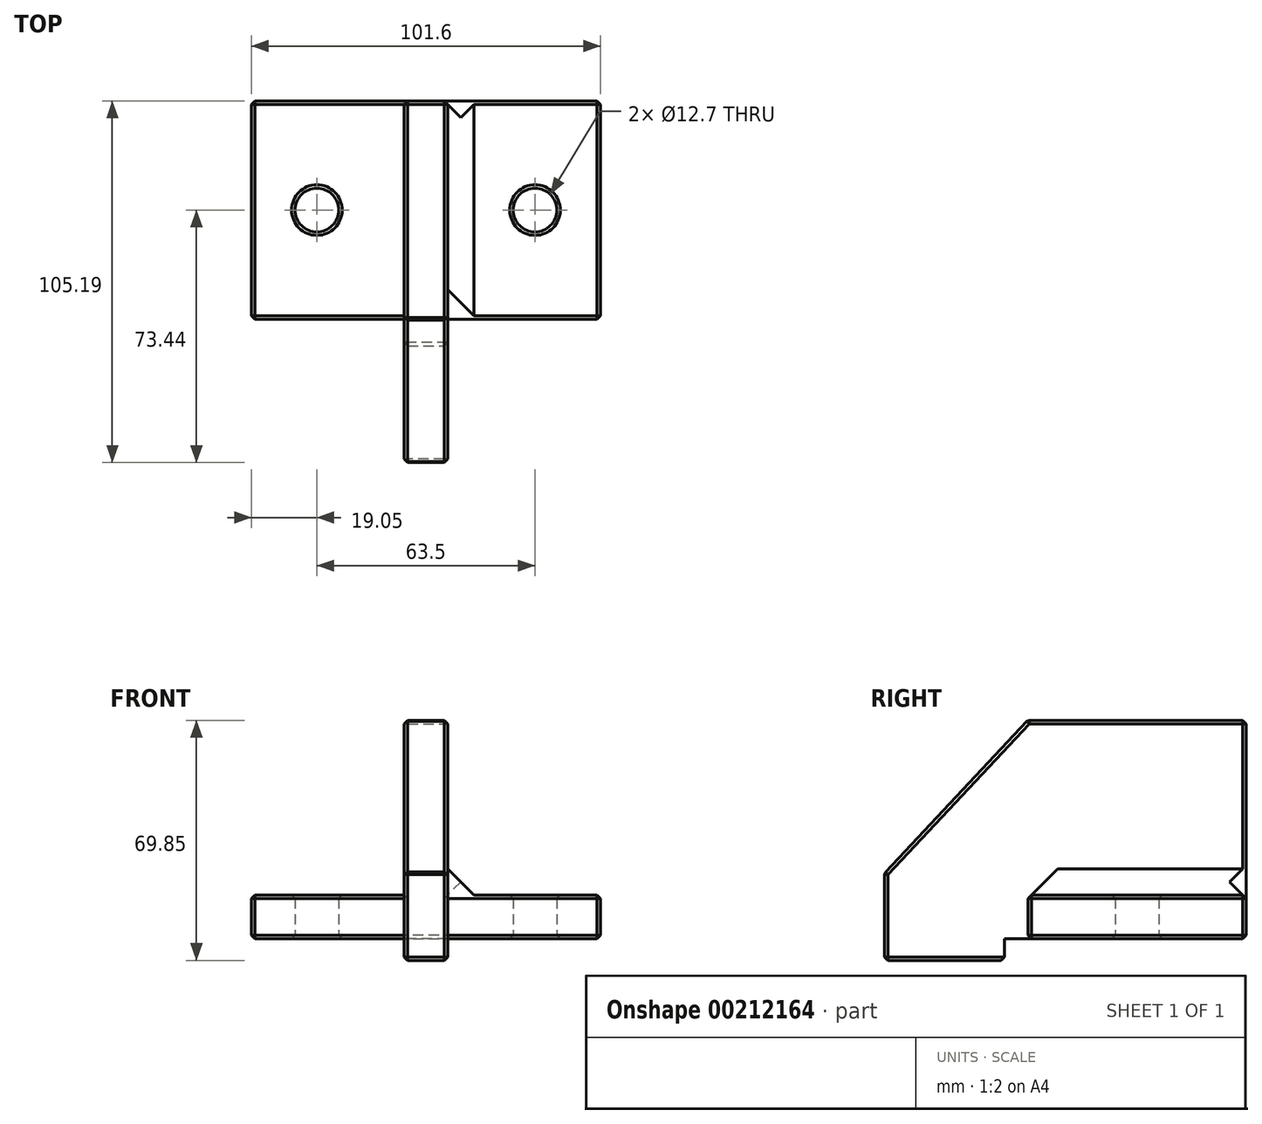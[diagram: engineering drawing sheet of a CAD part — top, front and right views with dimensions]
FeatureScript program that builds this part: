
annotation { "Feature Type Name" : "Feature", "Feature Type Description" : "" }
export const myFeature = defineFeature(function(context is Context, id is Id, definition is map)
    precondition{}
    {
        {
            var Q0;
            Q0=qCreatedBy(makeId("Top.planeOp"),FACE);
            var sketch = newSketch(context, id + "F0", { "sketchPlane" : qUnion([Q0])});
            skLineSegment(sketch, "E0.bottom", {"start": v(50.8, -31.75) * mm, "end": v(-50.8, -31.75) * mm});
            skLineSegment(sketch, "E0.top", {"start": v(50.8, 31.75) * mm, "end": v(-50.8, 31.75) * mm});
            skLineSegment(sketch, "E0.left", {"start": v(50.8, -31.75) * mm, "end": v(50.8, 31.75) * mm});
            skLineSegment(sketch, "E0.right", {"start": v(-50.8, -31.75) * mm, "end": v(-50.8, 31.75) * mm});
            skPoint(sketch, "E0.middle", {"position": v(0, 0) * mm});
            skCircle(sketch, "E1", {"center": v(-31.75, 0) * mm, "radius": 6.35 * mm});
            skCircle(sketch, "E2", {"center": v(31.75, 0) * mm, "radius": 6.35 * mm});
            skLineSegment(sketch, "E3", {"start": v(0, 0) * mm, "end": v(31.75, 0) * mm, "construction": true});
            skLineSegment(sketch, "E4", {"start": v(0, 0) * mm, "end": v(-31.75, 0) * mm, "construction": true});
            skSolve(sketch);
        }
        {
            var Q0;
            Q0=makeQuery(id+"F0.imprint","IMPRINT",FACE,{"disambiguationData":[TD([[makeQuery(id+"F0.imprint","IMPRINT",EDGE,{"derivedFrom":sQuery(id+"F0.wireOp",EDGE,"E0.bottom")}),-1.0]])]});
            extrude(context, id + "F1", {"entities" : qUnion([Q0]), "depth" : 12.7 * mm});
        }
        {
            var Q0;
            Q0=makeQuery(id+"F1.opExtrude","SWEPT_FACE",FACE,{"disambiguationData":[OSD([sQuery(id+"F0.wireOp",EDGE,"E0.right")])]});
            var sketch = newSketch(context, id + "F2", { "sketchPlane" : qUnion([Q0])});
            skLineSegment(sketch, "E5", {"start": v(-31.75, 12.7) * mm, "end": v(-31.75, 63.5) * mm});
            skLineSegment(sketch, "E6", {"start": v(-31.75, 63.5) * mm, "end": v(31.75, 63.5) * mm});
            skLineSegment(sketch, "E7", {"start": v(31.75, 63.5) * mm, "end": v(73.44, 19.05) * mm});
            skLineSegment(sketch, "E8", {"start": v(73.44, 19.05) * mm, "end": v(73.44, -6.35) * mm});
            skLineSegment(sketch, "E9", {"start": v(73.44, -6.35) * mm, "end": v(38.51, -6.35) * mm});
            skLineSegment(sketch, "E10", {"start": v(38.51, -6.35) * mm, "end": v(38.51, 0) * mm});
            skLineSegment(sketch, "E11", {"start": v(38.51, 0) * mm, "end": v(31.75, 0) * mm});
            skSolve(sketch);
        }
        {
            var Q0;
            Q0=makeQuery(id+"F2.imprint","IMPRINT",FACE,{"disambiguationData":[TD([[makeQuery(id+"F2.imprint","IMPRINT",EDGE,{"derivedFrom":sQuery(id+"F2.wireOp",EDGE,"E5")}),-1.0]])]});
            extrude(context, id + "F3", {"entities" : qUnion([Q0]), "operationType" : NewBodyOperationType.ADD, "oppositeDirection" : true, "depth" : 57.15 * mm, "hasSecondDirection" : true, "secondDirectionOppositeDirection" : true, "secondDirectionDepth" : 44.45 * mm});
        }
        {
            var Q0;
            Q0=makeQuery(id+"F3.opExtrude","SWEPT_EDGE",EDGE,{"disambiguationData":[OSD([sQuery(id+"F2.wireOp",EDGE,"E9"),sQuery(id+"F2.wireOp",EDGE,"E10")])]});
            var Q1;
            Q1=makeQuery(id+"F3.opExtrude","CAP_EDGE",EDGE,{"disambiguationData":[OSD([sQuery(id+"F2.wireOp",EDGE,"E9")])],"isStart":false});
            var Q2;
            Q2=makeQuery(id+"F3.opExtrude","CAP_EDGE",EDGE,{"disambiguationData":[OSD([sQuery(id+"F2.wireOp",EDGE,"E9")])],"isStart":true});
            var Q3;
            Q3=makeQuery(id+"F3.opExtrude","SWEPT_FACE",FACE,{"disambiguationData":[OSD([sQuery(id+"F2.wireOp",EDGE,"E8")])]});
            var Q4;
            Q4=makeQuery(id+"F3.opExtrude","SWEPT_FACE",FACE,{"disambiguationData":[OSD([sQuery(id+"F2.wireOp",EDGE,"E7")])]});
            var Q5;
            Q5=makeQuery(id+"F3.opExtrude","SWEPT_FACE",FACE,{"disambiguationData":[OSD([sQuery(id+"F2.wireOp",EDGE,"E6")])]});
            var Q6;
            Q6=makeQuery(id+"F3.boolean.opBoolean","MERGE",FACE,{"derivedFrom":[makeQuery(id+"F1.opExtrude","SWEPT_FACE",FACE,{"disambiguationData":[OSD([sQuery(id+"F0.wireOp",EDGE,"E0.top")])]}),makeQuery(id+"F3.opExtrude","SWEPT_FACE",FACE,{"disambiguationData":[OSD([sQuery(id+"F2.wireOp",EDGE,"E5")])]})]});
            var Q7;
            Q7=makeQuery(id+"F1.opExtrude","SWEPT_FACE",FACE,{"disambiguationData":[OSD([sQuery(id+"F0.wireOp",EDGE,"E0.right")])]});
            var Q8;
            {var subQ0=sQuery(id+"F0.wireOp",EDGE,"E0.bottom");var subQ1=sQuery(id+"F0.wireOp",EDGE,"E0.right");Q8=makeQuery(id+"F3.boolean.opBoolean","SPLIT",EDGE,{"disambiguationData":[TD([makeQuery(id+"F1.opExtrude","SWEPT_FACE",FACE,{"disambiguationData":[OSD([subQ1])]})])],"derivedFrom":makeQuery(id+"F1.opExtrude","CAP_EDGE",EDGE,{"disambiguationData":[OSD([subQ0])],"isStart":false})});}
            var Q9;
            {var subQ0=sQuery(id+"F0.wireOp",EDGE,"E0.bottom");var subQ1=sQuery(id+"F0.wireOp",EDGE,"E0.right");Q9=makeQuery(id+"F3.boolean.opBoolean","SPLIT",EDGE,{"disambiguationData":[TD([makeQuery(id+"F1.opExtrude","SWEPT_FACE",FACE,{"disambiguationData":[OSD([subQ1])]})])],"derivedFrom":makeQuery(id+"F1.opExtrude","CAP_EDGE",EDGE,{"disambiguationData":[OSD([subQ0])],"isStart":true})});}
            var Q10;
            Q10=makeQuery(id+"F1.opExtrude","SWEPT_FACE",FACE,{"disambiguationData":[OSD([sQuery(id+"F0.wireOp",EDGE,"E1")])]});
            var Q11;
            Q11=makeQuery(id+"F1.opExtrude","SWEPT_FACE",FACE,{"disambiguationData":[OSD([sQuery(id+"F0.wireOp",EDGE,"E2")])]});
            var Q12;
            {var subQ0=sQuery(id+"F0.wireOp",EDGE,"E0.bottom");var subQ2=sQuery(id+"F0.wireOp",EDGE,"E0.left");Q12=makeQuery(id+"F3.boolean.opBoolean","SPLIT",EDGE,{"disambiguationData":[TD([makeQuery(id+"F1.opExtrude","SWEPT_FACE",FACE,{"disambiguationData":[OSD([subQ2])]})])],"derivedFrom":makeQuery(id+"F1.opExtrude","CAP_EDGE",EDGE,{"disambiguationData":[OSD([subQ0])],"isStart":true})});}
            var Q13;
            Q13=makeQuery(id+"F1.opExtrude","SWEPT_EDGE",EDGE,{"disambiguationData":[OSD([sQuery(id+"F0.wireOp",EDGE,"E0.bottom"),sQuery(id+"F0.wireOp",EDGE,"E0.left")])]});
            var Q14;
            {var subQ0=sQuery(id+"F0.wireOp",EDGE,"E0.bottom");var subQ2=sQuery(id+"F0.wireOp",EDGE,"E0.left");Q14=makeQuery(id+"F3.boolean.opBoolean","SPLIT",EDGE,{"disambiguationData":[TD([makeQuery(id+"F1.opExtrude","SWEPT_FACE",FACE,{"disambiguationData":[OSD([subQ2])]})])],"derivedFrom":makeQuery(id+"F1.opExtrude","CAP_EDGE",EDGE,{"disambiguationData":[OSD([subQ0])],"isStart":false})});}
            var Q15;
            Q15=makeQuery(id+"F1.opExtrude","SWEPT_FACE",FACE,{"disambiguationData":[OSD([sQuery(id+"F0.wireOp",EDGE,"E0.left")])]});
            chamfer(context, id + "F4", {"entities" : qUnion([Q0, Q1, Q2, Q3, Q4, Q5, Q6, Q7, Q8, Q9, Q10, Q11, Q12, Q13, Q14, Q15]), "width" : 1.02 * mm, "tangentPropagation" : true});
        }
        {
            var Q0;
            {var subQ0=sQuery(id+"F0.wireOp",EDGE,"E0.right");Q0=makeQuery(id+"F3.opExtrude","CAP_EDGE",EDGE,{"disambiguationData":[OSD([subQ0]),TDD([makeQuery(id+"F2.imprint","IMPRINT",EDGE,{"derivedFrom":makeQuery(id+"F1.opExtrude","CAP_EDGE",EDGE,{"disambiguationData":[OSD([subQ0])],"isStart":false})})])],"isStart":false});}
            var Q1;
            {var subQ0=sQuery(id+"F0.wireOp",EDGE,"E0.right");Q1=makeQuery(id+"F3.opExtrude","CAP_EDGE",EDGE,{"disambiguationData":[OSD([subQ0]),TDD([makeQuery(id+"F2.imprint","IMPRINT",EDGE,{"derivedFrom":makeQuery(id+"F1.opExtrude","CAP_EDGE",EDGE,{"disambiguationData":[OSD([subQ0])],"isStart":false})})])],"isStart":true});}
            chamfer(context, id + "F5", {"entities" : qUnion([Q0, Q1]), "width" : 7.62 * mm, "tangentPropagation" : true});
        }
    });
